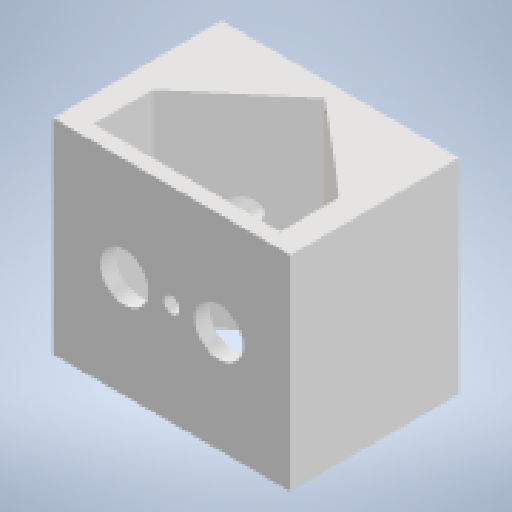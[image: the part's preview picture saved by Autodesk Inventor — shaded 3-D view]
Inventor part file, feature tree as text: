
AUTODESK INVENTOR PART (.ipt)
format: ipt  version: 2024.2 (Build 282272000, 272)  size: 212,480 bytes
history: native  units: mm
features: other x6, sketch x6, extrude x6, projected_geometry x2, reference x1
ambient origin geometry x8: Origin, YZ Plane, XZ Plane, XY Plane, X Axis, Y Axis, Z Axis, Center Point
bodies: Body1 (feature_tree)
feature tree (21):
  other  "Твердое тело1"
  other  "РабПлоскость2"
  sketch  "Эскиз1"
  extrude  "Выдавливание1"  Depth=4.0mm
  extrude  "Выдавливание2"  Depth=4.0mm
  other  "РабПлоскость4"
  extrude  "Выдавливание3"  Depth=4.0mm
  extrude  "Выдавливание4"  Depth=4.0mm
  extrude  "Выдавливание5"  Depth=3.0mm TaperAngle=0.0deg
  extrude  "Выдавливание6"  Depth=3.0mm TaperAngle=0.0deg
  reference  "Ссылка1"
  sketch  "Эскиз3"
  sketch  "Эскиз4"
  sketch  "Эскиз5"
  sketch  "Эскиз6"
  sketch  "Эскиз7"
  projected_geometry  "Спроецированная петля1"
  projected_geometry  "Спроецированная петля2"
  other  "<userpath>\Documents\Artist\3D\каретка.iam"
  other  "каретка.iam"
  other  "полное крепление каретки:1"
